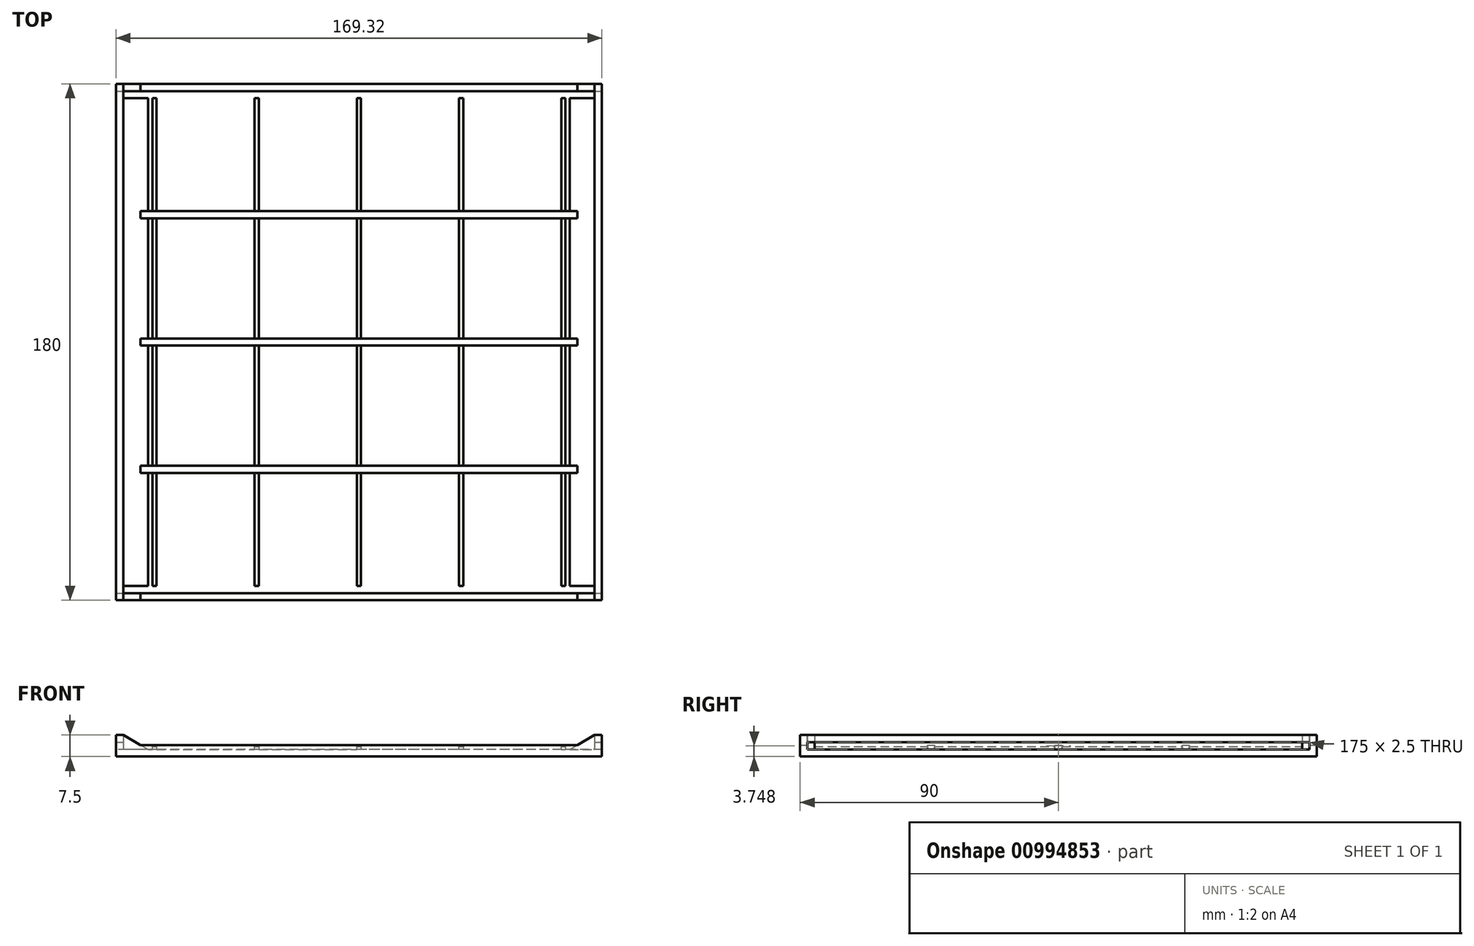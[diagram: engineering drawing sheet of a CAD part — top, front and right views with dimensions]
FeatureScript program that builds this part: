
annotation { "Feature Type Name" : "Feature", "Feature Type Description" : "" }
export const myFeature = defineFeature(function(context is Context, id is Id, definition is map)
    precondition{}
    {
        {
            var Q0;
            Q0=qCreatedBy(makeId("Front.planeOp"),FACE);
            var sketch = newSketch(context, id + "F0", { "sketchPlane" : qUnion([Q0])});
            skLineSegment(sketch, "E0", {"start": v(-64.58, 9.5) * mm, "end": v(20.08, 9.5) * mm});
            skLineSegment(sketch, "E1", {"start": v(20.08, 9.5) * mm, "end": v(20.08, 12) * mm});
            skLineSegment(sketch, "E2", {"start": v(20.08, 12) * mm, "end": v(17.58, 12) * mm});
            skLineSegment(sketch, "E3", {"start": v(17.58, 12) * mm, "end": v(17.58, 14.5) * mm});
            skLineSegment(sketch, "E4", {"start": v(17.58, 14.5) * mm, "end": v(20.08, 14.5) * mm});
            skLineSegment(sketch, "E5", {"start": v(20.08, 14.5) * mm, "end": v(20.08, 17) * mm});
            skLineSegment(sketch, "E6", {"start": v(20.08, 17) * mm, "end": v(17.58, 17) * mm});
            skLineSegment(sketch, "E7", {"start": v(17.58, 17) * mm, "end": v(8.92, 12) * mm});
            skLineSegment(sketch, "E8", {"start": v(8.92, 12) * mm, "end": v(-64.58, 12) * mm});
            skLineSegment(sketch, "E9", {"start": v(-64.58, 24.11) * mm, "end": v(-64.58, -2.27) * mm, "construction": true});
            skLineSegment(sketch, "E10.MirrorCS", {"start": v(-146.74, 14.5) * mm, "end": v(-149.24, 14.5) * mm});
            skLineSegment(sketch, "E11.MirrorCS", {"start": v(-149.24, 9.5) * mm, "end": v(-149.24, 12) * mm});
            skLineSegment(sketch, "E12.MirrorCS", {"start": v(-149.24, 12) * mm, "end": v(-146.74, 12) * mm});
            skLineSegment(sketch, "E13.MirrorCS", {"start": v(-146.74, 17) * mm, "end": v(-138.08, 12) * mm});
            skLineSegment(sketch, "E14.MirrorCS", {"start": v(-64.58, 9.5) * mm, "end": v(-149.24, 9.5) * mm});
            skLineSegment(sketch, "E15.MirrorCS", {"start": v(-146.74, 12) * mm, "end": v(-146.74, 14.5) * mm});
            skLineSegment(sketch, "E16.MirrorCS", {"start": v(-138.08, 12) * mm, "end": v(-64.58, 12) * mm});
            skLineSegment(sketch, "E17.MirrorCS", {"start": v(-149.24, 17) * mm, "end": v(-146.74, 17) * mm});
            skLineSegment(sketch, "E18.MirrorCS", {"start": v(-149.24, 14.5) * mm, "end": v(-149.24, 17) * mm});
            skSolve(sketch);
        }
        {
            var Q0;
            Q0=makeQuery(id+"F0.imprint","IMPRINT",FACE,{"disambiguationData":[TD([[makeQuery(id+"F0.imprint","IMPRINT",EDGE,{"derivedFrom":sQuery(id+"F0.wireOp",EDGE,"E0")}),1.0]])]});
            extrude(context, id + "F1", {"entities" : qUnion([Q0]), "oppositeDirection" : true, "depth" : 180 * mm, "offsetDistance" : 25 * mm});
        }
        {
            var Q0;
            Q0=makeQuery(id+"F1.opExtrude","SWEPT_FACE",FACE,{"disambiguationData":[OSD([sQuery(id+"F0.wireOp",EDGE,"E8"),sQuery(id+"F0.wireOp",EDGE,"E16.MirrorCS")])]});
            var sketch = newSketch(context, id + "F2", { "sketchPlane" : qUnion([Q0])});
            skCircle(sketch, "E19", {"center": v(-132.08, 169) * mm, "radius": 1.75 * mm});
            skCircle(sketch, "E20", {"center": v(-132.08, 64) * mm, "radius": 1.75 * mm});
            skCircle(sketch, "E21", {"center": v(2.92, 141) * mm, "radius": 1.75 * mm});
            skCircle(sketch, "E22", {"center": v(-78.08, 52.5) * mm, "radius": 1.75 * mm});
            skCircle(sketch, "E23", {"center": v(-78.08, 12) * mm, "radius": 1.75 * mm});
            skCircle(sketch, "E24", {"center": v(-6.48, 52.5) * mm, "radius": 1.75 * mm});
            skCircle(sketch, "E25", {"center": v(-6.48, 12) * mm, "radius": 1.75 * mm});
            skSolve(sketch);
        }
        {
            var Q0;
            Q0=makeQuery(id+"F1.opExtrude","SWEPT_FACE",FACE,{"disambiguationData":[OSD([sQuery(id+"F0.wireOp",EDGE,"E18.MirrorCS")])]});
            cPlane(context, id + "F3", {"entities" : qUnion([Q0]), "cplaneType" : CPlaneType.OFFSET, "offset" : 2.5 * mm, "oppositeDirection" : true, "width" : 150 * mm, "height" : 150 * mm});
        }
        {
            var Q0;
            Q0=qCreatedBy(id+"F3.planeOp",FACE);
            var sketch = newSketch(context, id + "F4", { "sketchPlane" : qUnion([Q0])});
            skLineSegment(sketch, "E26", {"start": v(-180, 13.5) * mm, "end": v(-180, 9.5) * mm});
            skLineSegment(sketch, "E27", {"start": v(-177.5, 9.5) * mm, "end": v(-177.5, 13.5) * mm});
            skLineSegment(sketch, "E28", {"start": v(-177.5, 13.5) * mm, "end": v(-180, 13.5) * mm});
            skLineSegment(sketch, "E29", {"start": v(-177.5, 9.5) * mm, "end": v(-180, 9.5) * mm});
            skLineSegment(sketch, "E30.1.0.0", {"start": v(-133.12, 9.5) * mm, "end": v(-133.12, 13.5) * mm});
            skLineSegment(sketch, "E30.1.0.1", {"start": v(-133.12, 9.5) * mm, "end": v(-135.62, 9.5) * mm});
            skLineSegment(sketch, "E30.1.0.2", {"start": v(-135.62, 13.5) * mm, "end": v(-135.62, 9.5) * mm});
            skLineSegment(sketch, "E30.1.0.3", {"start": v(-133.12, 13.5) * mm, "end": v(-135.62, 13.5) * mm});
            skLineSegment(sketch, "E30.2.0.0", {"start": v(-88.75, 9.5) * mm, "end": v(-88.75, 13.5) * mm});
            skLineSegment(sketch, "E30.2.0.1", {"start": v(-88.75, 9.5) * mm, "end": v(-91.25, 9.5) * mm});
            skLineSegment(sketch, "E30.2.0.2", {"start": v(-91.25, 13.5) * mm, "end": v(-91.25, 9.5) * mm});
            skLineSegment(sketch, "E30.2.0.3", {"start": v(-88.75, 13.5) * mm, "end": v(-91.25, 13.5) * mm});
            skLineSegment(sketch, "E30.3.0.0", {"start": v(-44.38, 9.5) * mm, "end": v(-44.38, 13.5) * mm});
            skLineSegment(sketch, "E30.3.0.1", {"start": v(-44.38, 9.5) * mm, "end": v(-46.88, 9.5) * mm});
            skLineSegment(sketch, "E30.3.0.2", {"start": v(-46.88, 13.5) * mm, "end": v(-46.88, 9.5) * mm});
            skLineSegment(sketch, "E30.3.0.3", {"start": v(-44.38, 13.5) * mm, "end": v(-46.88, 13.5) * mm});
            skLineSegment(sketch, "E30.4.0.0", {"start": v(0, 9.5) * mm, "end": v(0, 13.5) * mm});
            skLineSegment(sketch, "E30.4.0.1", {"start": v(0, 9.5) * mm, "end": v(-2.5, 9.5) * mm});
            skLineSegment(sketch, "E30.4.0.2", {"start": v(-2.5, 13.5) * mm, "end": v(-2.5, 9.5) * mm});
            skLineSegment(sketch, "E30.4.0.3", {"start": v(0, 13.5) * mm, "end": v(-2.5, 13.5) * mm});
            skLineSegment(sketch, "E30.direction1", {"start": v(-180, 9.5) * mm, "end": v(-135.62, 9.5) * mm, "construction": true});
            skSolve(sketch);
        }
        {
            var Q0;
            Q0 = qSketchRegion(id + "F4", true);
            extrude(context, id + "F5", {"entities" : qUnion([Q0]), "operationType" : NewBodyOperationType.ADD, "oppositeDirection" : true, "depth" : 164 * mm, "offsetDistance" : 25 * mm});
        }
        {
            var Q0;
            Q0=makeQuery(id+"F1.opExtrude","SWEPT_FACE",FACE,{"disambiguationData":[OSD([sQuery(id+"F0.wireOp",EDGE,"E0"),sQuery(id+"F0.wireOp",EDGE,"E14.MirrorCS")])]});
            var sketch = newSketch(context, id + "F6", { "sketchPlane" : qUnion([Q0])});
            skLineSegment(sketch, "E31", {"start": v(-146.74, 0) * mm, "end": v(-146.74, -2.5) * mm});
            skLineSegment(sketch, "E32", {"start": v(-146.74, -2.5) * mm, "end": v(-149.24, -2.5) * mm});
            skLineSegment(sketch, "E33", {"start": v(-149.24, -2.5) * mm, "end": v(-149.24, 0) * mm});
            skLineSegment(sketch, "E34", {"start": v(-149.24, 0) * mm, "end": v(-146.74, 0) * mm});
            skLineSegment(sketch, "E35", {"start": v(-64.58, 0) * mm, "end": v(-64.58, -180) * mm, "construction": true});
            skLineSegment(sketch, "E36", {"start": v(20.08, -90) * mm, "end": v(-149.24, -90) * mm, "construction": true});
            skLineSegment(sketch, "E37.MirrorCS", {"start": v(17.58, -2.5) * mm, "end": v(20.08, -2.5) * mm});
            skLineSegment(sketch, "E38.MirrorCS", {"start": v(20.08, 0) * mm, "end": v(17.58, 0) * mm});
            skLineSegment(sketch, "E39.MirrorCS", {"start": v(17.58, 0) * mm, "end": v(17.58, -2.5) * mm});
            skLineSegment(sketch, "E40.MirrorCS", {"start": v(20.08, -2.5) * mm, "end": v(20.08, 0) * mm});
            skLineSegment(sketch, "E41.MirrorCS", {"start": v(17.58, -180) * mm, "end": v(17.58, -177.5) * mm});
            skLineSegment(sketch, "E42.MirrorCS", {"start": v(20.08, -180) * mm, "end": v(17.58, -180) * mm});
            skLineSegment(sketch, "E43.MirrorCS", {"start": v(17.58, -177.5) * mm, "end": v(20.08, -177.5) * mm});
            skLineSegment(sketch, "E44.MirrorCS", {"start": v(20.08, -177.5) * mm, "end": v(20.08, -180) * mm});
            skLineSegment(sketch, "E45.MirrorCS", {"start": v(-146.74, -180) * mm, "end": v(-146.74, -177.5) * mm});
            skLineSegment(sketch, "E46.MirrorCS", {"start": v(-149.24, -177.5) * mm, "end": v(-149.24, -180) * mm});
            skLineSegment(sketch, "E47.MirrorCS", {"start": v(-146.74, -177.5) * mm, "end": v(-149.24, -177.5) * mm});
            skLineSegment(sketch, "E48.MirrorCS", {"start": v(-149.24, -180) * mm, "end": v(-146.74, -180) * mm});
            skSolve(sketch);
        }
        {
            var Q0;
            Q0 = qSketchRegion(id + "F6", true);
            extrude(context, id + "F7", {"entities" : qUnion([Q0]), "operationType" : NewBodyOperationType.ADD, "oppositeDirection" : true, "depth" : 7.5 * mm, "offsetDistance" : 25 * mm});
        }
        {
            var Q0;
            Q0=makeQuery(id+"F2.imprint","IMPRINT",FACE,{"disambiguationData":[TD([[makeQuery(id+"F2.imprint","IMPRINT",EDGE,{"derivedFrom":sQuery(id+"F2.wireOp",EDGE,"E19")}),-1.0]])]});
            var sketch = newSketch(context, id + "F8", { "sketchPlane" : qUnion([Q0])});
            skLineSegment(sketch, "E49.0.0", {"start": v(-138.08, 0) * mm, "end": v(8.92, 0) * mm, "construction": true});
            skLineSegment(sketch, "E49.0.1", {"start": v(8.92, 0) * mm, "end": v(8.92, 180) * mm, "construction": true});
            skLineSegment(sketch, "E49.0.2", {"start": v(8.92, 180) * mm, "end": v(-138.08, 180) * mm, "construction": true});
            skLineSegment(sketch, "E49.0.3", {"start": v(-138.08, 180) * mm, "end": v(-138.08, 0) * mm, "construction": true});
            skLineSegment(sketch, "E50", {"start": v(-64.58, 0) * mm, "end": v(-64.58, 180) * mm, "construction": true});
            skLineSegment(sketch, "E51", {"start": v(8.92, 90) * mm, "end": v(-138.08, 90) * mm, "construction": true});
            skLineSegment(sketch, "E52", {"start": v(-136.74, 175) * mm, "end": v(-146.74, 175) * mm});
            skLineSegment(sketch, "E53", {"start": v(-136.74, 175) * mm, "end": v(-136.74, 177.5) * mm});
            skLineSegment(sketch, "E54", {"start": v(-136.74, 177.5) * mm, "end": v(-146.74, 177.5) * mm});
            skLineSegment(sketch, "E55", {"start": v(-146.74, 177.5) * mm, "end": v(-146.74, 175) * mm});
            skLineSegment(sketch, "E56.0", {"start": v(-146.74, 180) * mm, "end": v(-146.74, 0) * mm});
            skLineSegment(sketch, "E57.MirrorCS", {"start": v(7.58, 175) * mm, "end": v(7.58, 177.5) * mm});
            skLineSegment(sketch, "E58.MirrorCS", {"start": v(7.58, 177.5) * mm, "end": v(17.58, 177.5) * mm});
            skLineSegment(sketch, "E59.MirrorCS", {"start": v(17.58, 177.5) * mm, "end": v(17.58, 175) * mm});
            skLineSegment(sketch, "E60.MirrorCS", {"start": v(7.58, 175) * mm, "end": v(17.58, 175) * mm});
            skLineSegment(sketch, "E61.MirrorCS", {"start": v(-146.74, 2.5) * mm, "end": v(-146.74, 5) * mm});
            skLineSegment(sketch, "E62.MirrorCS", {"start": v(7.58, 2.5) * mm, "end": v(17.58, 2.5) * mm});
            skLineSegment(sketch, "E63.MirrorCS", {"start": v(-136.74, 2.5) * mm, "end": v(-146.74, 2.5) * mm});
            skLineSegment(sketch, "E64.MirrorCS", {"start": v(7.58, 5) * mm, "end": v(7.58, 2.5) * mm});
            skLineSegment(sketch, "E65.MirrorCS", {"start": v(17.58, 2.5) * mm, "end": v(17.58, 5) * mm});
            skLineSegment(sketch, "E66.MirrorCS", {"start": v(-136.74, 5) * mm, "end": v(-136.74, 2.5) * mm});
            skLineSegment(sketch, "E67.MirrorCS", {"start": v(7.58, 5) * mm, "end": v(17.58, 5) * mm});
            skLineSegment(sketch, "E68.MirrorCS", {"start": v(8.92, 0) * mm, "end": v(-138.08, 0) * mm, "construction": true});
            skLineSegment(sketch, "E69.MirrorCS", {"start": v(-136.74, 5) * mm, "end": v(-146.74, 5) * mm});
            skSolve(sketch);
        }
        {
            var Q0;
            Q0 = qSketchRegion(id + "F8", true);
            extrude(context, id + "F9", {"entities" : qUnion([Q0]), "operationType" : NewBodyOperationType.REMOVE, "depth" : 25 * mm, "offsetDistance" : 25 * mm});
        }
        {
            var Q0;
            Q0=makeQuery(id+"F9.boolean.opBoolean","COPY",FACE,{"derivedFrom":makeQuery(id+"F9.opExtrude","SWEPT_FACE",FACE,{"disambiguationData":[OSD([sQuery(id+"F8.wireOp",EDGE,"E60.MirrorCS")])]})});
            var sketch = newSketch(context, id + "F10", { "sketchPlane" : qUnion([Q0])});
            skLineSegment(sketch, "E70", {"start": v(-7.42, 13) * mm, "end": v(-5.92, 13) * mm});
            skLineSegment(sketch, "E71", {"start": v(-5.92, 13) * mm, "end": v(-5.92, 12) * mm});
            skLineSegment(sketch, "E72", {"start": v(-5.92, 12) * mm, "end": v(-7.42, 12) * mm});
            skLineSegment(sketch, "E73", {"start": v(-7.42, 12) * mm, "end": v(-7.42, 13) * mm});
            skLineSegment(sketch, "E74.0", {"start": v(-8.92, 12) * mm, "end": v(138.08, 12) * mm});
            skLineSegment(sketch, "E75.1.0.0", {"start": v(29.7, 12) * mm, "end": v(28.2, 12) * mm});
            skLineSegment(sketch, "E75.1.0.1", {"start": v(28.2, 13) * mm, "end": v(29.7, 13) * mm});
            skLineSegment(sketch, "E75.1.0.2", {"start": v(29.7, 13) * mm, "end": v(29.7, 12) * mm});
            skLineSegment(sketch, "E75.1.0.3", {"start": v(28.2, 12) * mm, "end": v(28.2, 13) * mm});
            skLineSegment(sketch, "E75.2.0.0", {"start": v(65.33, 12) * mm, "end": v(63.83, 12) * mm});
            skLineSegment(sketch, "E75.2.0.1", {"start": v(63.83, 13) * mm, "end": v(65.33, 13) * mm});
            skLineSegment(sketch, "E75.2.0.2", {"start": v(65.33, 13) * mm, "end": v(65.33, 12) * mm});
            skLineSegment(sketch, "E75.2.0.3", {"start": v(63.83, 12) * mm, "end": v(63.83, 13) * mm});
            skLineSegment(sketch, "E75.3.0.0", {"start": v(100.95, 12) * mm, "end": v(99.45, 12) * mm});
            skLineSegment(sketch, "E75.3.0.1", {"start": v(99.45, 13) * mm, "end": v(100.95, 13) * mm});
            skLineSegment(sketch, "E75.3.0.2", {"start": v(100.95, 13) * mm, "end": v(100.95, 12) * mm});
            skLineSegment(sketch, "E75.3.0.3", {"start": v(99.45, 12) * mm, "end": v(99.45, 13) * mm});
            skLineSegment(sketch, "E75.4.0.0", {"start": v(136.58, 12) * mm, "end": v(135.08, 12) * mm});
            skLineSegment(sketch, "E75.4.0.1", {"start": v(135.08, 13) * mm, "end": v(136.58, 13) * mm});
            skLineSegment(sketch, "E75.4.0.2", {"start": v(136.58, 13) * mm, "end": v(136.58, 12) * mm});
            skLineSegment(sketch, "E75.4.0.3", {"start": v(135.08, 12) * mm, "end": v(135.08, 13) * mm});
            skLineSegment(sketch, "E75.direction1", {"start": v(-7.42, 12) * mm, "end": v(28.2, 12) * mm, "construction": true});
            skSolve(sketch);
        }
        {
            var Q0;
            Q0 = qSketchRegion(id + "F10", true);
            extrude(context, id + "F11", {"entities" : qUnion([Q0]), "operationType" : NewBodyOperationType.ADD, "oppositeDirection" : true, "depth" : 170 * mm, "offsetDistance" : 25 * mm});
        }
    });
